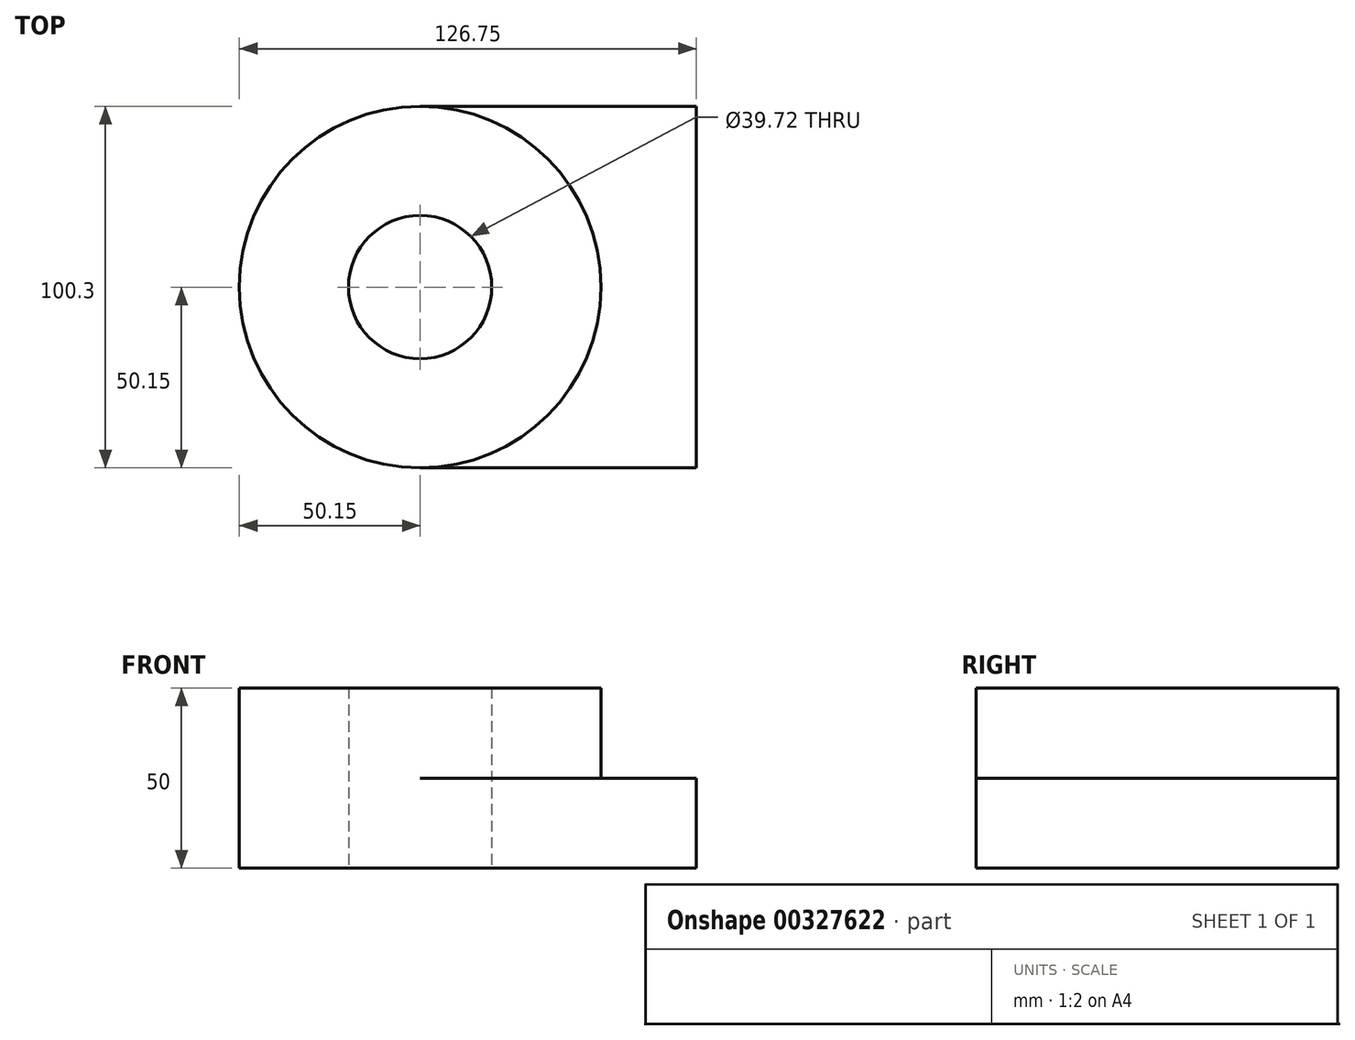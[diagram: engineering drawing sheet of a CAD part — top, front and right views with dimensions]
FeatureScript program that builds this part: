
annotation { "Feature Type Name" : "Feature", "Feature Type Description" : "" }
export const myFeature = defineFeature(function(context is Context, id is Id, definition is map)
    precondition{}
    {
        {
            var Q0;
            Q0=qCreatedBy(makeId("Top.planeOp"),FACE);
            var sketch = newSketch(context, id + "F0", { "sketchPlane" : qUnion([Q0])});
            skCircle(sketch, "E0", {"center": v(0, 0) * mm, "radius": 50.15 * mm});
            skLineSegment(sketch, "E1.bottom", {"start": v(0, 50.15) * mm, "end": v(76.6, 50.15) * mm});
            skLineSegment(sketch, "E1.top", {"start": v(0, -50.15) * mm, "end": v(76.6, -50.15) * mm});
            skLineSegment(sketch, "E1.right", {"start": v(76.6, 50.15) * mm, "end": v(76.6, -50.15) * mm});
            skCircle(sketch, "E2", {"center": v(0, 0) * mm, "radius": 19.86 * mm});
            skSolve(sketch);
        }
        {
            var Q0;
            Q0=makeQuery(id+"F0.imprint","IMPRINT",FACE,{"disambiguationData":[TD([[makeQuery(id+"F0.imprint","IMPRINT",EDGE,{"derivedFrom":sQuery(id+"F0.wireOp",EDGE,"E2")}),-1.0]])]});
            extrude(context, id + "F1", {"entities" : qUnion([Q0]), "depth" : 50 * mm});
        }
        {
            var Q0;
            Q0 = qSketchRegion(id + "F0", true);
            extrude(context, id + "F2", {"entities" : qUnion([Q0]), "operationType" : NewBodyOperationType.ADD, "depth" : 25 * mm});
        }
    });
